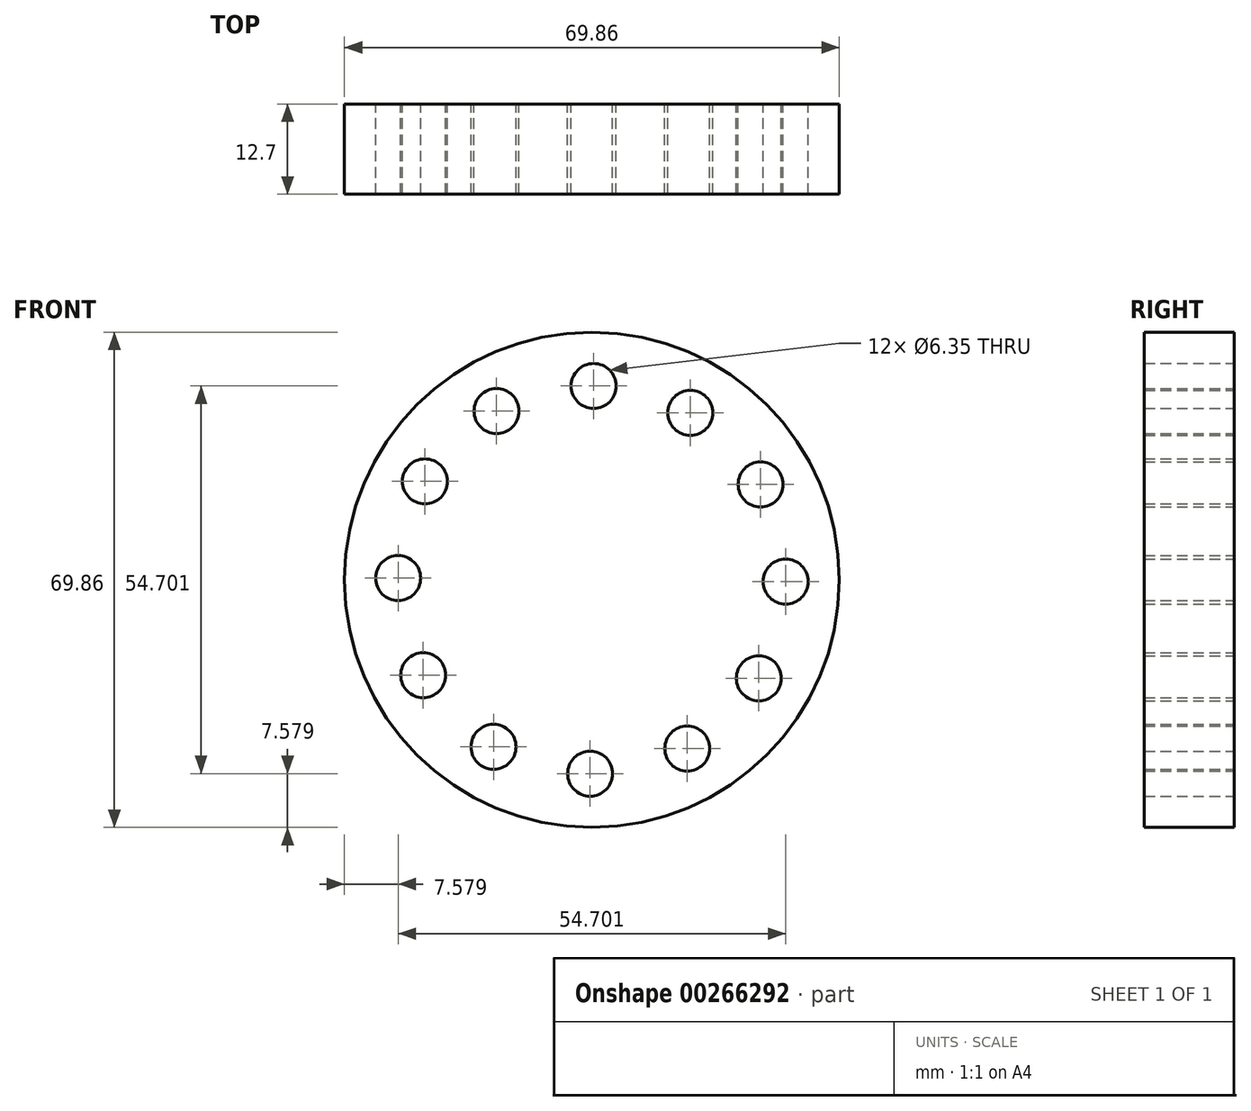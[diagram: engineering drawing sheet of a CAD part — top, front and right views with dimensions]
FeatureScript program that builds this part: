
annotation { "Feature Type Name" : "Feature", "Feature Type Description" : "" }
export const myFeature = defineFeature(function(context is Context, id is Id, definition is map)
    precondition{}
    {
        {
            var Q0;
            Q0=qCreatedBy(makeId("Front.planeOp"),FACE);
            var sketch = newSketch(context, id + "F0", { "sketchPlane" : qUnion([Q0])});
            skCircle(sketch, "E0", {"center": v(0, 0) * mm, "radius": 34.93 * mm});
            skCircle(sketch, "E1", {"center": v(-27.35, 0.25) * mm, "radius": 3.18 * mm});
            skCircle(sketch, "E2.1.0", {"center": v(-23.81, -13.46) * mm, "radius": 3.18 * mm});
            skCircle(sketch, "E2.2.0", {"center": v(-13.89, -23.56) * mm, "radius": 3.18 * mm});
            skCircle(sketch, "E2.3.0", {"center": v(-0.25, -27.35) * mm, "radius": 3.18 * mm});
            skCircle(sketch, "E2.4.0", {"center": v(13.46, -23.81) * mm, "radius": 3.18 * mm});
            skCircle(sketch, "E2.5.0", {"center": v(23.56, -13.89) * mm, "radius": 3.18 * mm});
            skCircle(sketch, "E2.6.0", {"center": v(27.35, -0.25) * mm, "radius": 3.18 * mm});
            skCircle(sketch, "E2.7.0", {"center": v(23.81, 13.46) * mm, "radius": 3.18 * mm});
            skCircle(sketch, "E2.8.0", {"center": v(13.89, 23.56) * mm, "radius": 3.18 * mm});
            skCircle(sketch, "E2.9.0", {"center": v(0.25, 27.35) * mm, "radius": 3.18 * mm});
            skCircle(sketch, "E2.10.0", {"center": v(-13.46, 23.81) * mm, "radius": 3.18 * mm});
            skCircle(sketch, "E2.11.0", {"center": v(-23.56, 13.89) * mm, "radius": 3.18 * mm});
            skSolve(sketch);
        }
        {
            var Q0;
            Q0=makeQuery(id+"F0.imprint","IMPRINT",FACE,{"disambiguationData":[TD([[makeQuery(id+"F0.imprint","IMPRINT",EDGE,{"derivedFrom":sQuery(id+"F0.wireOp",EDGE,"E0")}),1.0]])]});
            extrude(context, id + "F1", {"entities" : qUnion([Q0]), "depth" : 12.7 * mm});
        }
    });
